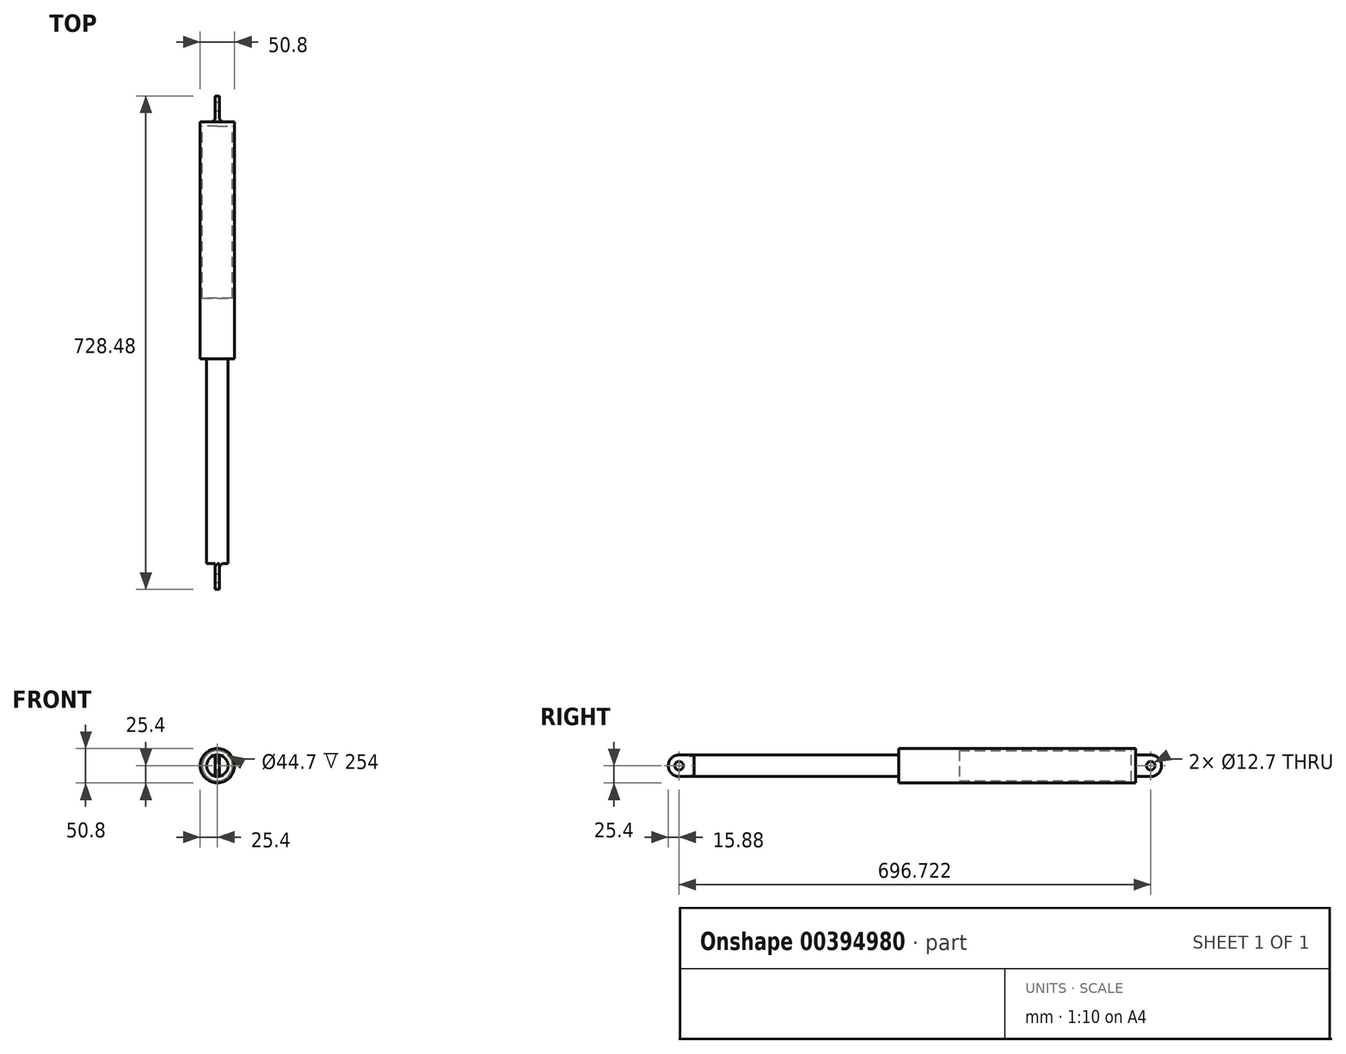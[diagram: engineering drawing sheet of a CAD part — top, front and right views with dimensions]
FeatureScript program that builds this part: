
annotation { "Feature Type Name" : "Feature", "Feature Type Description" : "" }
export const myFeature = defineFeature(function(context is Context, id is Id, definition is map)
    precondition{}
    {
        {
            var Q0;
            Q0=qCreatedBy(makeId("Right.planeOp"),FACE);
            var sketch = newSketch(context, id + "F0", { "sketchPlane" : qUnion([Q0])});
            skArc(sketch, "E0", {"start": v(0, 15.88) * mm, "mid": v(-15.88, 0) * mm, "end": v(0, -15.88) * mm});
            skLineSegment(sketch, "E1", {"start": v(0, 15.88) * mm, "end": v(22.22, 15.88) * mm});
            skLineSegment(sketch, "E2", {"start": v(22.22, 15.88) * mm, "end": v(22.23, -15.88) * mm});
            skCircle(sketch, "E3", {"center": v(0, 0) * mm, "radius": 6.35 * mm});
            skLineSegment(sketch, "E4", {"start": v(0, -15.88) * mm, "end": v(22.23, -15.88) * mm});
            skSolve(sketch);
        }
        {
            var Q0;
            Q0=qSketchRegion(id+"F0",true);
            extrude(context, id + "F1", {"entities" : qUnion([Q0]), "endBound" : BoundingType.SYMMETRIC, "depth" : 6.35 * mm});
        }
        {
            var Q0;
            Q0=makeQuery(id+"F1.opExtrude","SWEPT_FACE",FACE,{"disambiguationData":[OSD([sQuery(id+"F0.wireOp",EDGE,"E2")])]});
            var sketch = newSketch(context, id + "F2", { "sketchPlane" : qUnion([Q0])});
            skCircle(sketch, "E5", {"center": v(0, 0) * mm, "radius": 15.88 * mm});
            skSolve(sketch);
        }
        {
            var Q0;
            Q0=qSketchRegion(id+"F2",true);
            extrude(context, id + "F3", {"entities" : qUnion([Q0]), "operationType" : NewBodyOperationType.ADD, "depth" : 375 * mm + 16.92 * mm});
        }
        {
            var Q0;
            {var subQ0=sQuery(id+"F0.wireOp",EDGE,"E2");Q0=makeQuery(id+"F3.boolean.opBoolean","SPLIT",EDGE,{"disambiguationData":[topologyDisambiguationEdgeConnected([makeQuery(id+"F1.opExtrude","CAP_FACE",FACE,{"disambiguationData":[OSD([sQuery(id+"F0.wireOp",EDGE,"E0"),sQuery(id+"F0.wireOp",EDGE,"E1"),subQ0,sQuery(id+"F0.wireOp",EDGE,"E3"),sQuery(id+"F0.wireOp",EDGE,"E4")])],"isStart":false}),makeQuery(id+"F3.opExtrude","CAP_FACE",FACE,{"disambiguationData":[OSD([sQuery(id+"F2.wireOp",EDGE,"E5")])],"isStart":true})])],"derivedFrom":makeQuery(id+"F1.opExtrude","CAP_EDGE",EDGE,{"disambiguationData":[OSD([subQ0])],"isStart":false})});}
            var Q1;
            {var subQ0=sQuery(id+"F0.wireOp",EDGE,"E2");Q1=makeQuery(id+"F3.boolean.opBoolean","SPLIT",EDGE,{"disambiguationData":[topologyDisambiguationEdgeConnected([makeQuery(id+"F1.opExtrude","CAP_FACE",FACE,{"disambiguationData":[OSD([sQuery(id+"F0.wireOp",EDGE,"E0"),sQuery(id+"F0.wireOp",EDGE,"E1"),subQ0,sQuery(id+"F0.wireOp",EDGE,"E3"),sQuery(id+"F0.wireOp",EDGE,"E4")])],"isStart":true}),makeQuery(id+"F3.opExtrude","CAP_FACE",FACE,{"disambiguationData":[OSD([sQuery(id+"F2.wireOp",EDGE,"E5")])],"isStart":true})])],"derivedFrom":makeQuery(id+"F1.opExtrude","CAP_EDGE",EDGE,{"disambiguationData":[OSD([subQ0])],"isStart":true})});}
            fillet(context, id + "F4", {"entities" : qUnion([Q0, Q1]), "radius" : 6.35 * mm, "tangentPropagation" : true, "allowEdgeOverflow" : false});
        }
        {
            var Q0;
            Q0=qCreatedBy(makeId("Right.planeOp"),FACE);
            var sketch = newSketch(context, id + "F5", { "sketchPlane" : qUnion([Q0])});
            skCircle(sketch, "E6", {"center": v(696.72, 0) * mm, "radius": 6.35 * mm});
            skArc(sketch, "E7", {"start": v(696.72, -15.87) * mm, "mid": v(712.6, 0) * mm, "end": v(696.72, 15.88) * mm});
            skLineSegment(sketch, "E8", {"start": v(696.72, 15.88) * mm, "end": v(674.5, 15.88) * mm});
            skLineSegment(sketch, "E9", {"start": v(674.5, 15.88) * mm, "end": v(674.5, -15.88) * mm});
            skLineSegment(sketch, "E10", {"start": v(696.72, -15.88) * mm, "end": v(674.5, -15.88) * mm});
            skSolve(sketch);
        }
        {
            var Q0;
            Q0=qSketchRegion(id+"F5",true);
            extrude(context, id + "F6", {"entities" : qUnion([Q0]), "endBound" : BoundingType.SYMMETRIC, "depth" : 6.35 * mm});
        }
        {
            var Q0;
            Q0=makeQuery(id+"F6.opExtrude","SWEPT_FACE",FACE,{"disambiguationData":[OSD([sQuery(id+"F5.wireOp",EDGE,"E9")])]});
            var sketch = newSketch(context, id + "F7", { "sketchPlane" : qUnion([Q0])});
            skCircle(sketch, "E11", {"center": v(0, 0) * mm, "radius": 25.4 * mm});
            skCircle(sketch, "E12.0.0", {"center": v(0, 0) * mm, "radius": 15.88 * mm, "construction": true});
            skCircle(sketch, "E13", {"center": v(0, 0) * mm, "radius": 22.35 * mm});
            skSolve(sketch);
        }
        {
            var Q0;
            Q0=qSketchRegion(id+"F7",true);
            extrude(context, id + "F8", {"entities" : qUnion([Q0]), "depth" : 350 * mm});
        }
        {
            var Q0;
            Q0=makeQuery(id+"F6.opExtrude","SWEPT_FACE",FACE,{"disambiguationData":[OSD([sQuery(id+"F5.wireOp",EDGE,"E9")])]});
            var sketch = newSketch(context, id + "F9", { "sketchPlane" : qUnion([Q0])});
            skCircle(sketch, "E14.0", {"center": v(0, 0) * mm, "radius": 22.35 * mm});
            skSolve(sketch);
        }
        {
            var Q0;
            Q0=qSketchRegion(id+"F9",true);
            extrude(context, id + "F10", {"entities" : qUnion([Q0]), "operationType" : NewBodyOperationType.ADD, "depth" : 6.35 * mm});
        }
        {
            var Q0;
            {var subQ0=sQuery(id+"F5.wireOp",EDGE,"E9");Q0=makeQuery(id+"F10.boolean.opBoolean","SPLIT",EDGE,{"disambiguationData":[topologyDisambiguationEdgeConnected([makeQuery(id+"F6.opExtrude","CAP_FACE",FACE,{"disambiguationData":[OSD([sQuery(id+"F5.wireOp",EDGE,"E6"),sQuery(id+"F5.wireOp",EDGE,"E7"),sQuery(id+"F5.wireOp",EDGE,"E8"),subQ0,sQuery(id+"F5.wireOp",EDGE,"E10")])],"isStart":true}),makeQuery(id+"F10.opExtrude","CAP_FACE",FACE,{"disambiguationData":[OSD([sQuery(id+"F9.wireOp",EDGE,"0a1f69fb-0a38-4f9e-a69e-4767d570a797.0")])],"isStart":true})])],"derivedFrom":makeQuery(id+"F6.opExtrude","CAP_EDGE",EDGE,{"disambiguationData":[OSD([subQ0])],"isStart":true})});}
            var Q1;
            {var subQ0=sQuery(id+"F5.wireOp",EDGE,"E9");Q1=makeQuery(id+"F10.boolean.opBoolean","SPLIT",EDGE,{"disambiguationData":[topologyDisambiguationEdgeConnected([makeQuery(id+"F6.opExtrude","CAP_FACE",FACE,{"disambiguationData":[OSD([sQuery(id+"F5.wireOp",EDGE,"E6"),sQuery(id+"F5.wireOp",EDGE,"E7"),sQuery(id+"F5.wireOp",EDGE,"E8"),subQ0,sQuery(id+"F5.wireOp",EDGE,"E10")])],"isStart":false}),makeQuery(id+"F10.opExtrude","CAP_FACE",FACE,{"disambiguationData":[OSD([sQuery(id+"F9.wireOp",EDGE,"0a1f69fb-0a38-4f9e-a69e-4767d570a797.0")])],"isStart":true})])],"derivedFrom":makeQuery(id+"F6.opExtrude","CAP_EDGE",EDGE,{"disambiguationData":[OSD([subQ0])],"isStart":false})});}
            fillet(context, id + "F11", {"entities" : qUnion([Q0, Q1]), "radius" : 6.35 * mm, "tangentPropagation" : true, "allowEdgeOverflow" : false});
        }
        {
            var Q0;
            Q0=makeQuery(id+"F8.opExtrude","CAP_FACE",FACE,{"disambiguationData":[OSD([sQuery(id+"F7.wireOp",EDGE,"E11"),sQuery(id+"F7.wireOp",EDGE,"E13")])],"isStart":false});
            var sketch = newSketch(context, id + "F12", { "sketchPlane" : qUnion([Q0])});
            skCircle(sketch, "E15.0", {"center": v(0, 0) * mm, "radius": 22.35 * mm});
            skCircle(sketch, "E16.0", {"center": v(0, 0) * mm, "radius": 15.88 * mm});
            skSolve(sketch);
        }
        {
            var Q0;
            Q0=qSketchRegion(id+"F12",true);
            extrude(context, id + "F13", {"entities" : qUnion([Q0]), "operationType" : NewBodyOperationType.ADD, "oppositeDirection" : true, "depth" : 6.35 * mm});
        }
        {
            var Q0;
            Q0=makeQuery(id+"F3.opExtrude","CAP_FACE",FACE,{"disambiguationData":[OSD([sQuery(id+"F2.wireOp",EDGE,"E5")])],"isStart":false});
            var sketch = newSketch(context, id + "F14", { "sketchPlane" : qUnion([Q0])});
            skCircle(sketch, "E17.0", {"center": v(0, 0) * mm, "radius": 25.4 * mm, "construction": true});
            skCircle(sketch, "E18", {"center": v(0, 0) * mm, "radius": 22.35 * mm});
            skCircle(sketch, "E19.0", {"center": v(0, 0) * mm, "radius": 15.88 * mm});
            skSolve(sketch);
        }
        {
            var Q0;
            Q0=qSketchRegion(id+"F14",true);
            extrude(context, id + "F15", {"entities" : qUnion([Q0]), "operationType" : NewBodyOperationType.ADD, "endBound" : BoundingType.UP_TO_NEXT, "oppositeDirection" : true, "depth" : 25 * mm});
        }
    });
